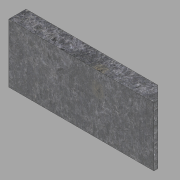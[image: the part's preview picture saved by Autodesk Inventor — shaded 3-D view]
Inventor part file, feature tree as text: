
AUTODESK INVENTOR PART (.ipt)
format: ipt  version: 2022.2 (Build 262287000, 287)  size: 143,872 bytes
history: native  units: in
note: dims shown in document units (in); Inventor stores cm internally (conversion verified against a paired STEP export)
features: extrude x4, sketch x4, thicken_offset x1
ambient origin geometry x8: Origin, YZ Plane, XZ Plane, XY Plane, X Axis, Y Axis, Z Axis, Center Point
bodies: Solid1 (feature_tree)
feature tree (9):
  extrude  "Extrusion1"  Depth=7.625in
  extrude  "Extrusion3"  Depth=18.8125in TaperAngle=0.0deg
  thicken_offset  "Thicken1"
  extrude  "Extrusion4"  Depth=0.125in
  extrude  "Extrusion5"  Depth=7.625in
  sketch  "Sketch1"  dims[d0=2.25in d1=7.625in]
  sketch  "Sketch3"  dims[d2=18.8125in d3=0.0in d10=1.0in d11=0.0in]
  sketch  "Sketch4"  dims[d12=0.125in d13=0.125in]
  sketch  "Sketch6"  dims[d15=7.625in d16=0.0in d17=0.5in d18=0.6765in d19=0.0in]
